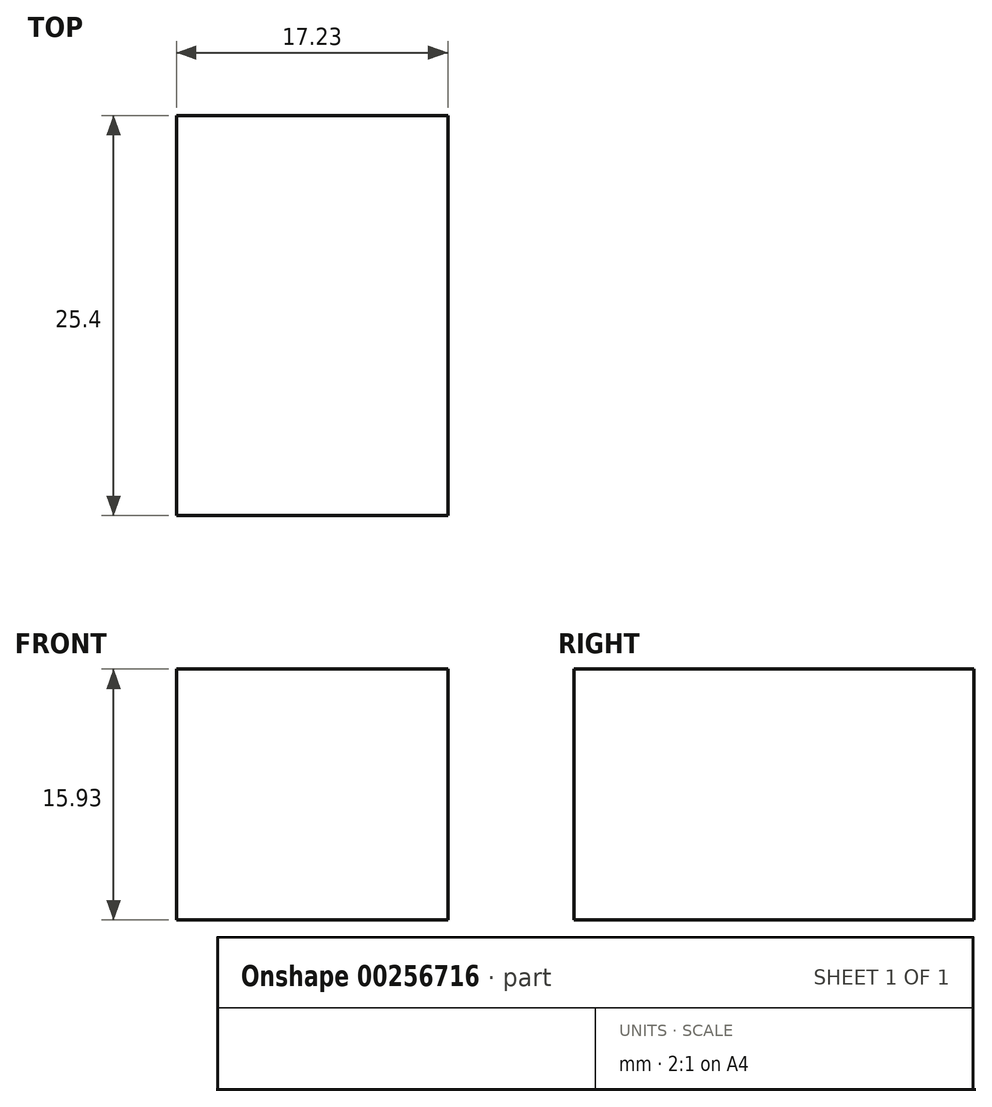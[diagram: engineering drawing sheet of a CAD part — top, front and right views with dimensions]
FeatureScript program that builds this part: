
annotation { "Feature Type Name" : "Feature", "Feature Type Description" : "" }
export const myFeature = defineFeature(function(context is Context, id is Id, definition is map)
    precondition{}
    {
        {
            var Q0;
            Q0=qCreatedBy(makeId("Front.planeOp"),FACE);
            var sketch = newSketch(context, id + "F0", { "sketchPlane" : qUnion([Q0])});
            skLineSegment(sketch, "E0.bottom", {"start": v(-46.8, 32.97) * mm, "end": v(-64.03, 32.97) * mm});
            skLineSegment(sketch, "E0.top", {"start": v(-46.8, 48.9) * mm, "end": v(-64.03, 48.9) * mm});
            skLineSegment(sketch, "E0.left", {"start": v(-46.8, 32.97) * mm, "end": v(-46.8, 48.9) * mm});
            skLineSegment(sketch, "E0.right", {"start": v(-64.03, 32.97) * mm, "end": v(-64.03, 48.9) * mm});
            skPoint(sketch, "E0.middle", {"position": v(-55.42, 40.93) * mm});
            skSolve(sketch);
        }
        {
            var Q0;
            Q0 = qSketchRegion(id + "F0", true);
            extrude(context, id + "F1", {"entities" : qUnion([Q0]), "depth" : 25.4 * mm});
        }
    });
